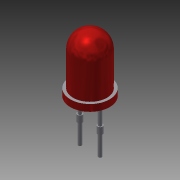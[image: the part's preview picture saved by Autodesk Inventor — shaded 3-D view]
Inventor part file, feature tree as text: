
AUTODESK INVENTOR PART (.ipt)
format: ipt  version: 2013 SP1 (Build 170176100, 176)  size: 135,168 bytes
history: native  units: mm
features: sketch x6, extrude x4, other x2, mirror x2, fillet x1
ambient origin geometry x8: Origin, YZ Plane, XZ Plane, XY Plane, X Axis, Y Axis, Z Axis, Center Point
bodies: Volumenkörper1 (feature_tree), Volumenkörper2 (feature_tree), Volumenkörper3 (feature_tree)
feature tree (15):
  extrude  "Extrusion1"  Depth=7.5mm TaperAngle=0.0deg
  fillet  "Rundung1"  Radius=2.5mm
  extrude  "Extrusion2"  Depth=1.0mm TaperAngle=0.0deg
  sketch  "Skizze Helper"  dims[d24=1.0mm d25=0.0mm d26=0.0mm d27=0.0mm d28=-4.0mm]
  extrude  "Extrusion Bein"  Depth=0.5mm
  other  "Körper verschieben Bein"
  extrude  "Extrusion Lötpunkt"  TaperAngle=0.0deg  [1 undecoded]
  other  "Körper verschieben Lötpunkt"
  sketch  "Skizze Helper2"  dims[d4=5.8mm d5=1.0mm d6=0.0mm]
  mirror  "Spiegeln1"
  mirror  "Spiegeln2"
  sketch  "Skizze1"  dims[d0=5.0mm d1=7.5mm d2=0.0mm d3=2.5mm]
  sketch  "Skizze2"  dims[d12=3.0mm d13=0.5mm]
  sketch  "Skizze5"  dims[d14=7.0mm d15=0.0mm d19=0.0mm d20=0.0mm d21=-1.0mm]
  sketch  "Skizze7"  dims[d23=0.75mm]
note: 1 required parameter value undecoded (feature->parameter linkage not recoverable at this tier; creation-order binding heuristic only, values carry confidence <= 0.55)
